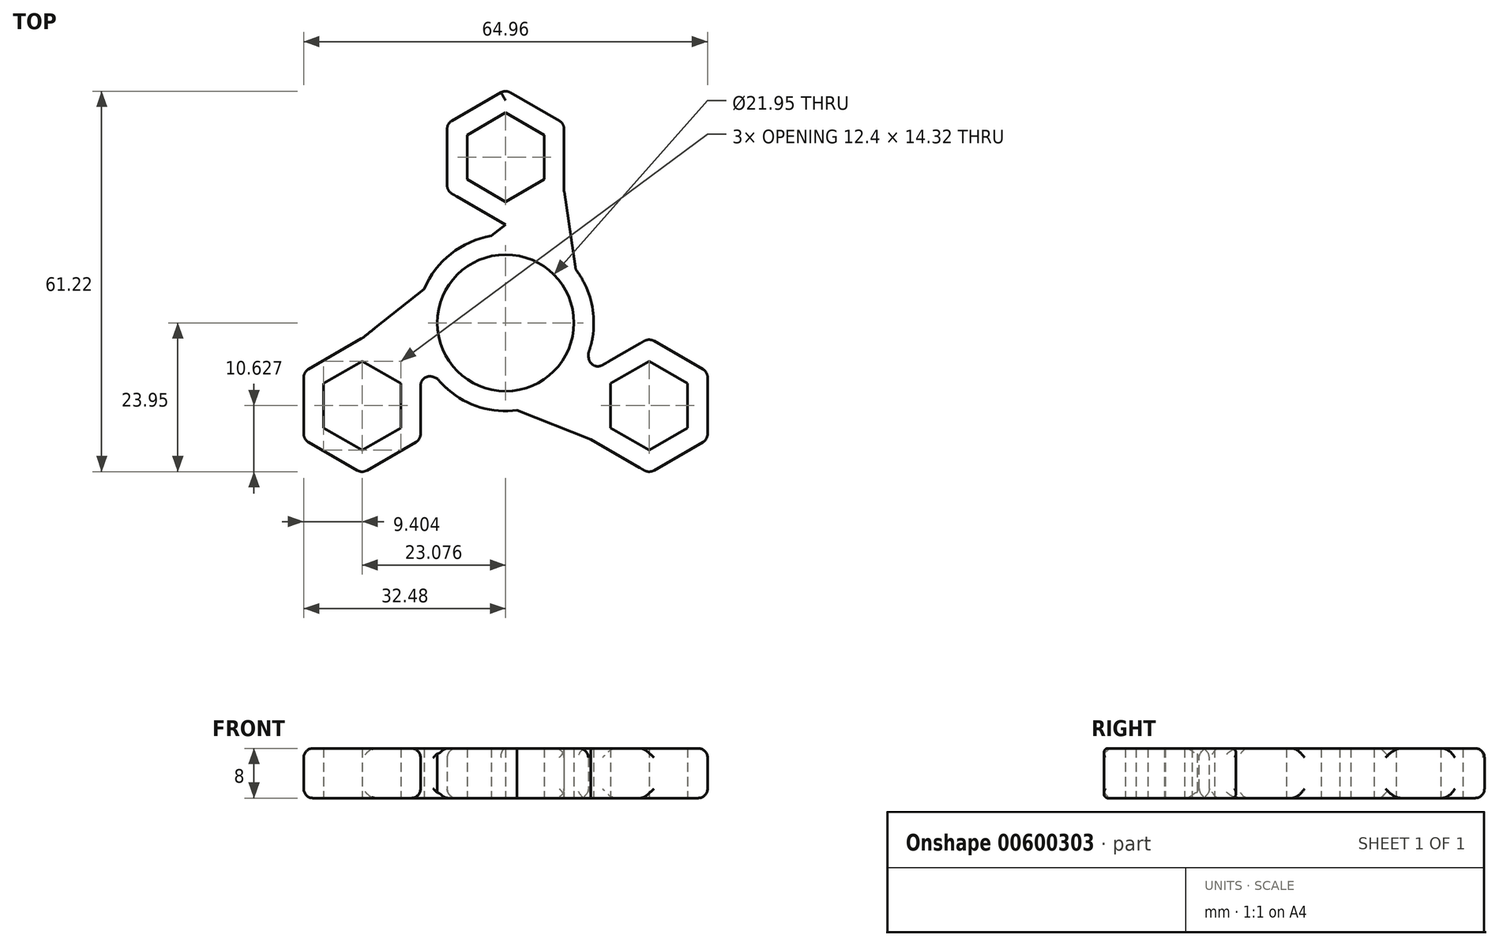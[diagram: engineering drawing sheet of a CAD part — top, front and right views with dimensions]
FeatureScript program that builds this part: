
annotation { "Feature Type Name" : "Feature", "Feature Type Description" : "" }
export const myFeature = defineFeature(function(context is Context, id is Id, definition is map)
    precondition{}
    {
        {
            var Q0;
            Q0=qCreatedBy(makeId("Top.planeOp"),FACE);
            var sketch = newSketch(context, id + "F0", { "sketchPlane" : qUnion([Q0])});
            skLineSegment(sketch, "E0", {"start": v(0, 26.65) * mm, "end": v(0, 0) * mm, "construction": true});
            skLineSegment(sketch, "E1", {"start": v(0, 0) * mm, "end": v(-23.08, -13.32) * mm, "construction": true});
            skLineSegment(sketch, "E2", {"start": v(0, 0) * mm, "end": v(23.08, -13.32) * mm, "construction": true});
            skCircle(sketch, "E3.cCircle", {"center": v(0, 26.65) * mm, "radius": 6.2 * mm, "construction": true});
            skLineSegment(sketch, "E3.0", {"start": v(6.2, 23.07) * mm, "end": v(0, 19.49) * mm});
            skLineSegment(sketch, "E3.1", {"start": v(0, 19.49) * mm, "end": v(-6.2, 23.07) * mm});
            skLineSegment(sketch, "E3.2", {"start": v(-6.2, 23.07) * mm, "end": v(-6.2, 30.23) * mm});
            skLineSegment(sketch, "E3.3", {"start": v(-6.2, 30.23) * mm, "end": v(0, 33.8) * mm});
            skLineSegment(sketch, "E3.4", {"start": v(0, 33.8) * mm, "end": v(6.2, 30.23) * mm});
            skLineSegment(sketch, "E3.5", {"start": v(6.2, 30.23) * mm, "end": v(6.2, 23.07) * mm});
            skPoint(sketch, "E3.0.midPoint", {"position": v(3.1, 21.28) * mm});
            skCircle(sketch, "E4.cCircle", {"center": v(0, 26.65) * mm, "radius": 9.4 * mm, "construction": true});
            skLineSegment(sketch, "E4.0", {"start": v(9.4, 21.22) * mm, "end": v(0, 15.8) * mm});
            skLineSegment(sketch, "E4.1", {"start": v(0, 15.8) * mm, "end": v(-9.4, 21.22) * mm});
            skLineSegment(sketch, "E4.2", {"start": v(-9.4, 21.22) * mm, "end": v(-9.4, 32.07) * mm});
            skLineSegment(sketch, "E4.3", {"start": v(-9.4, 32.07) * mm, "end": v(0, 37.5) * mm});
            skLineSegment(sketch, "E4.4", {"start": v(0, 37.5) * mm, "end": v(9.4, 32.07) * mm});
            skLineSegment(sketch, "E4.5", {"start": v(9.4, 32.07) * mm, "end": v(9.4, 21.22) * mm});
            skPoint(sketch, "E4.0.midPoint", {"position": v(4.7, 18.5) * mm});
            skCircle(sketch, "E5", {"center": v(0, 0) * mm, "radius": 10.97 * mm});
            skCircle(sketch, "E6.cCircle", {"center": v(23.08, -13.32) * mm, "radius": 6.2 * mm, "construction": true});
            skLineSegment(sketch, "E6.0", {"start": v(29.28, -16.9) * mm, "end": v(23.08, -20.48) * mm});
            skLineSegment(sketch, "E6.1", {"start": v(23.08, -20.48) * mm, "end": v(16.88, -16.9) * mm});
            skLineSegment(sketch, "E6.2", {"start": v(16.88, -16.9) * mm, "end": v(16.88, -9.74) * mm});
            skLineSegment(sketch, "E6.3", {"start": v(16.88, -9.74) * mm, "end": v(23.08, -6.16) * mm});
            skLineSegment(sketch, "E6.4", {"start": v(23.08, -6.16) * mm, "end": v(29.28, -9.74) * mm});
            skLineSegment(sketch, "E6.5", {"start": v(29.28, -9.74) * mm, "end": v(29.28, -16.9) * mm});
            skPoint(sketch, "E6.0.midPoint", {"position": v(26.18, -18.7) * mm});
            skCircle(sketch, "E7.cCircle", {"center": v(23.08, -13.32) * mm, "radius": 9.4 * mm, "construction": true});
            skLineSegment(sketch, "E7.0", {"start": v(32.48, -18.75) * mm, "end": v(23.08, -24.18) * mm});
            skLineSegment(sketch, "E7.1", {"start": v(23.08, -24.18) * mm, "end": v(13.68, -18.75) * mm});
            skLineSegment(sketch, "E7.2", {"start": v(13.68, -18.75) * mm, "end": v(13.68, -7.9) * mm});
            skLineSegment(sketch, "E7.3", {"start": v(13.68, -7.9) * mm, "end": v(23.08, -2.47) * mm});
            skLineSegment(sketch, "E7.4", {"start": v(23.08, -2.47) * mm, "end": v(32.48, -7.9) * mm});
            skLineSegment(sketch, "E7.5", {"start": v(32.48, -7.9) * mm, "end": v(32.48, -18.75) * mm});
            skPoint(sketch, "E7.0.midPoint", {"position": v(27.78, -21.46) * mm});
            skCircle(sketch, "E8.cCircle", {"center": v(-23.08, -13.32) * mm, "radius": 6.2 * mm, "construction": true});
            skLineSegment(sketch, "E8.0", {"start": v(-16.88, -16.9) * mm, "end": v(-23.08, -20.48) * mm});
            skLineSegment(sketch, "E8.1", {"start": v(-23.08, -20.48) * mm, "end": v(-29.28, -16.9) * mm});
            skLineSegment(sketch, "E8.2", {"start": v(-29.28, -16.9) * mm, "end": v(-29.28, -9.74) * mm});
            skLineSegment(sketch, "E8.3", {"start": v(-29.28, -9.74) * mm, "end": v(-23.08, -6.16) * mm});
            skLineSegment(sketch, "E8.4", {"start": v(-23.08, -6.16) * mm, "end": v(-16.88, -9.74) * mm});
            skLineSegment(sketch, "E8.5", {"start": v(-16.88, -9.74) * mm, "end": v(-16.88, -16.9) * mm});
            skPoint(sketch, "E8.0.midPoint", {"position": v(-19.98, -18.7) * mm});
            skCircle(sketch, "E9.cCircle", {"center": v(-23.08, -13.32) * mm, "radius": 9.4 * mm, "construction": true});
            skLineSegment(sketch, "E9.0", {"start": v(-13.68, -18.75) * mm, "end": v(-23.08, -24.18) * mm});
            skLineSegment(sketch, "E9.1", {"start": v(-23.08, -24.18) * mm, "end": v(-32.48, -18.75) * mm});
            skLineSegment(sketch, "E9.2", {"start": v(-32.48, -18.75) * mm, "end": v(-32.48, -7.9) * mm});
            skLineSegment(sketch, "E9.3", {"start": v(-32.48, -7.9) * mm, "end": v(-23.08, -2.47) * mm});
            skLineSegment(sketch, "E9.4", {"start": v(-23.08, -2.47) * mm, "end": v(-13.68, -7.9) * mm});
            skLineSegment(sketch, "E9.5", {"start": v(-13.68, -7.9) * mm, "end": v(-13.68, -18.75) * mm});
            skPoint(sketch, "E9.0.midPoint", {"position": v(-18.38, -21.46) * mm});
            skCircle(sketch, "E10", {"center": v(0, 0) * mm, "radius": 14.18 * mm});
            skCircle(sketch, "E11", {"center": v(0, 0) * mm, "radius": 37.5 * mm, "construction": true});
            skLineSegment(sketch, "E12", {"start": v(-23.08, -2.47) * mm, "end": v(0, 15.8) * mm});
            skLineSegment(sketch, "E13", {"start": v(9.4, 21.22) * mm, "end": v(13.68, -7.9) * mm});
            skLineSegment(sketch, "E14", {"start": v(13.68, -18.75) * mm, "end": v(-13.68, -7.9) * mm});
            skSolve(sketch);
        }
        {
            var Q0;
            Q0=qSketchRegion(id+"F0",true);
            extrude(context, id + "F1", {"entities" : qUnion([Q0]), "endBound" : BoundingType.SYMMETRIC, "depth" : 8 * mm, "offsetDistance" : 25 * mm});
        }
        {
            var Q0;
            Q0=makeQuery(id+"F1.opExtrude","SWEPT_FACE",FACE,{"disambiguationData":[OSD([sQuery(id+"F0.wireOp",EDGE,"E9.0")])]});
            var Q1;
            Q1=makeQuery(id+"F1.opExtrude","SWEPT_FACE",FACE,{"disambiguationData":[OSD([sQuery(id+"F0.wireOp",EDGE,"E9.5")])]});
            var Q2;
            {var subQ0=sQuery(id+"F0.wireOp",EDGE,"E14");Q2=makeQuery(id+"F1.opExtrude","SWEPT_FACE",FACE,{"disambiguationData":[OSD([subQ0]),TDD([makeQuery(id+"F0.imprint","IMPRINT",EDGE,{"disambiguationData":[TD([[makeQuery(id+"F0.imprint","INTERSECT",VERTEX,{"disambiguationData":[OD(0.0)],"derivedFrom":[sQuery(id+"F0.wireOp",EDGE,"E10"),subQ0]}),-1.0]])],"derivedFrom":subQ0})])]});}
            var Q3;
            {var subQ0=sQuery(id+"F0.wireOp",EDGE,"E14");Q3=makeQuery(id+"F1.opExtrude","SWEPT_FACE",FACE,{"disambiguationData":[OSD([subQ0]),TDD([makeQuery(id+"F0.imprint","IMPRINT",EDGE,{"disambiguationData":[TD([[makeQuery(id+"F0.imprint","INTERSECT",VERTEX,{"disambiguationData":[OD(1.0)],"derivedFrom":[sQuery(id+"F0.wireOp",EDGE,"E10"),subQ0]}),1.0]])],"derivedFrom":subQ0})])]});}
            var Q4;
            Q4=makeQuery(id+"F1.opExtrude","SWEPT_FACE",FACE,{"disambiguationData":[OSD([sQuery(id+"F0.wireOp",EDGE,"E7.0")])]});
            var Q5;
            Q5=makeQuery(id+"F1.opExtrude","SWEPT_FACE",FACE,{"disambiguationData":[OSD([sQuery(id+"F0.wireOp",EDGE,"E7.5")])]});
            var Q6;
            Q6=makeQuery(id+"F1.opExtrude","SWEPT_FACE",FACE,{"disambiguationData":[OSD([sQuery(id+"F0.wireOp",EDGE,"E7.4")])]});
            var Q7;
            {var subQ0=sQuery(id+"F0.wireOp",EDGE,"E13");Q7=makeQuery(id+"F1.opExtrude","SWEPT_FACE",FACE,{"disambiguationData":[OSD([subQ0]),TDD([makeQuery(id+"F0.imprint","IMPRINT",EDGE,{"disambiguationData":[TD([[makeQuery(id+"F0.imprint","INTERSECT",VERTEX,{"disambiguationData":[OD(1.0)],"derivedFrom":[sQuery(id+"F0.wireOp",EDGE,"E10"),subQ0]}),-1.0]])],"derivedFrom":subQ0})])]});}
            var Q8;
            {var subQ0=sQuery(id+"F0.wireOp",EDGE,"E13");Q8=makeQuery(id+"F1.opExtrude","SWEPT_FACE",FACE,{"disambiguationData":[OSD([subQ0]),TDD([makeQuery(id+"F0.imprint","IMPRINT",EDGE,{"disambiguationData":[TD([[makeQuery(id+"F0.imprint","INTERSECT",VERTEX,{"disambiguationData":[OD(0.0)],"derivedFrom":[sQuery(id+"F0.wireOp",EDGE,"E10"),subQ0]}),1.0]])],"derivedFrom":subQ0})])]});}
            var Q9;
            Q9=makeQuery(id+"F1.opExtrude","SWEPT_FACE",FACE,{"disambiguationData":[OSD([sQuery(id+"F0.wireOp",EDGE,"E4.3")])]});
            var Q10;
            Q10=makeQuery(id+"F1.opExtrude","SWEPT_FACE",FACE,{"disambiguationData":[OSD([sQuery(id+"F0.wireOp",EDGE,"E4.4")])]});
            var Q11;
            {var subQ0=sQuery(id+"F0.wireOp",EDGE,"E12");Q11=makeQuery(id+"F1.opExtrude","SWEPT_FACE",FACE,{"disambiguationData":[OSD([subQ0]),TDD([makeQuery(id+"F0.imprint","IMPRINT",EDGE,{"disambiguationData":[TD([[makeQuery(id+"F0.imprint","INTERSECT",VERTEX,{"disambiguationData":[OD(0.0)],"derivedFrom":[sQuery(id+"F0.wireOp",EDGE,"E10"),subQ0]}),-1.0]])],"derivedFrom":subQ0})])]});}
            var Q12;
            Q12=makeQuery(id+"F1.opExtrude","SWEPT_FACE",FACE,{"disambiguationData":[OSD([sQuery(id+"F0.wireOp",EDGE,"E4.2")])]});
            var Q13;
            Q13=makeQuery(id+"F1.opExtrude","SWEPT_FACE",FACE,{"disambiguationData":[OSD([sQuery(id+"F0.wireOp",EDGE,"E9.3")])]});
            var Q14;
            Q14=makeQuery(id+"F1.opExtrude","SWEPT_FACE",FACE,{"disambiguationData":[OSD([sQuery(id+"F0.wireOp",EDGE,"E9.2")])]});
            var Q15;
            Q15=makeQuery(id+"F1.opExtrude","SWEPT_FACE",FACE,{"disambiguationData":[OSD([sQuery(id+"F0.wireOp",EDGE,"E9.1")])]});
            fillet(context, id + "F2", {"entities" : qUnion([Q0, Q1, Q2, Q3, Q4, Q5, Q6, Q7, Q8, Q9, Q10, Q11, Q12, Q13, Q14, Q15]), "radius" : 1.5 * mm, "tangentPropagation" : true, "allowEdgeOverflow" : false});
        }
    });
